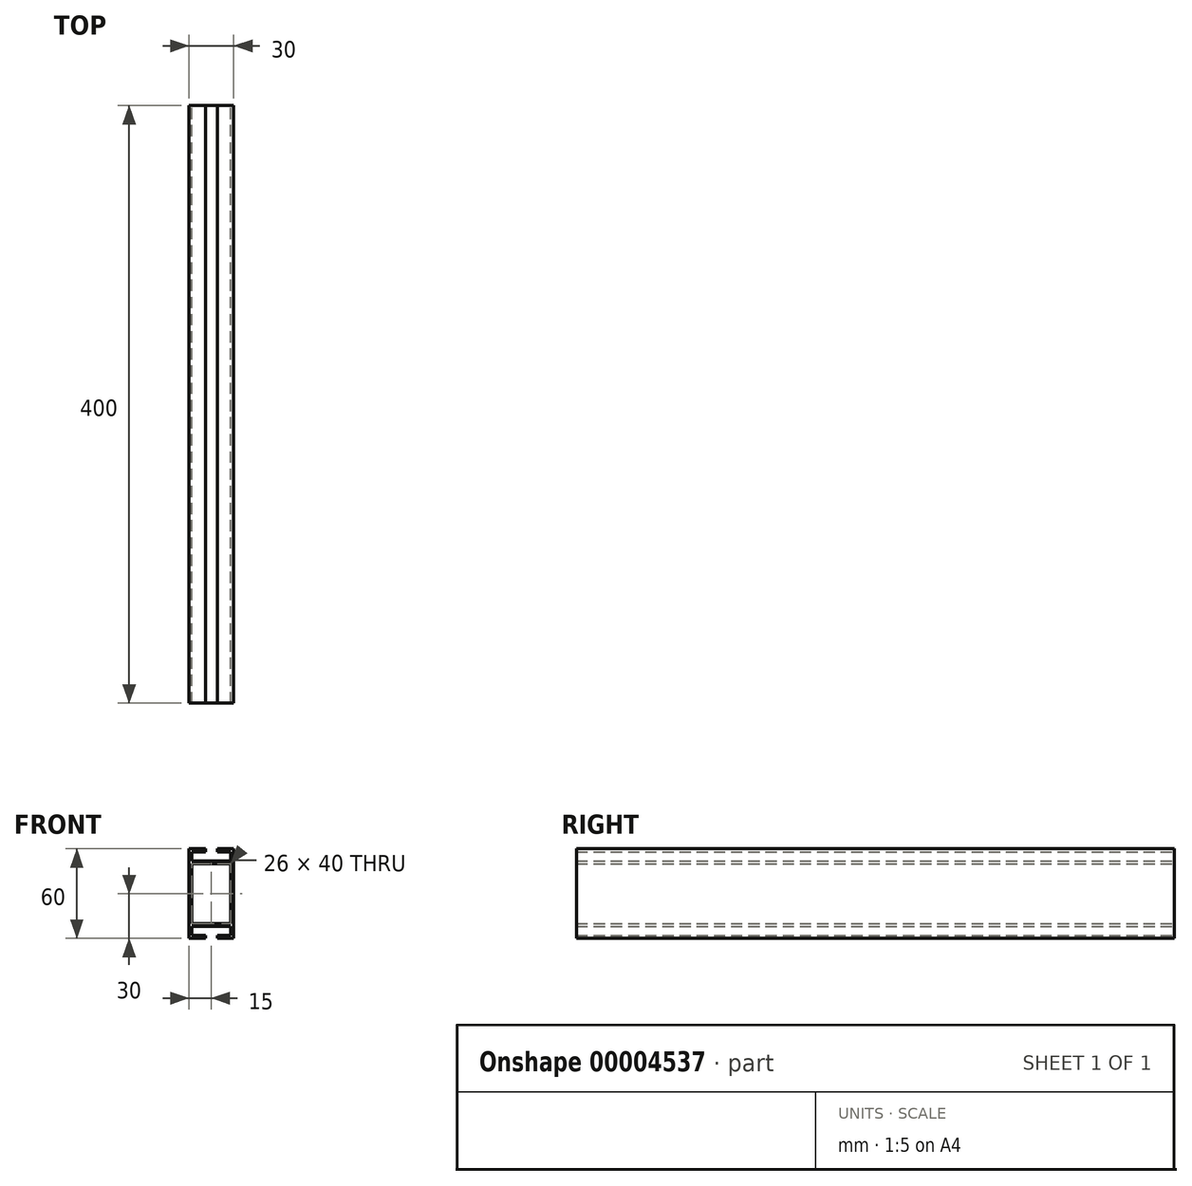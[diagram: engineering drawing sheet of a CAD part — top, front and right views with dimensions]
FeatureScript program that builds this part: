
annotation { "Feature Type Name" : "Feature", "Feature Type Description" : "" }
export const myFeature = defineFeature(function(context is Context, id is Id, definition is map)
    precondition{}
    {
        {
            var Q0;
            Q0=qCreatedBy(makeId("Front.planeOp"),FACE);
            var sketch = newSketch(context, id + "F0", { "sketchPlane" : qUnion([Q0])});
            skLineSegment(sketch, "E0.rect.bottom", {"start": v(15, 30) * mm, "end": v(4, 30) * mm});
            skLineSegment(sketch, "E0.rect.top", {"start": v(15, -30) * mm, "end": v(4, -30) * mm});
            skLineSegment(sketch, "E0.rect.left", {"start": v(15, 30) * mm, "end": v(15, -30) * mm});
            skLineSegment(sketch, "E0.rect.right", {"start": v(-15, 30) * mm, "end": v(-15, -30) * mm});
            skPoint(sketch, "E0.rect.middle", {"position": v(0, 0) * mm});
            skLineSegment(sketch, "E1.0", {"start": v(13, 28) * mm, "end": v(4, 28) * mm});
            skLineSegment(sketch, "E1.1", {"start": v(13, 28) * mm, "end": v(13, -22) * mm});
            skLineSegment(sketch, "E1.2", {"start": v(13, -28) * mm, "end": v(4, -28) * mm});
            skLineSegment(sketch, "E1.3", {"start": v(-13, 28) * mm, "end": v(-13, 22) * mm});
            skLineSegment(sketch, "E2.rect.bottom", {"start": v(13, 22) * mm, "end": v(-13, 22) * mm});
            skLineSegment(sketch, "E2.rect.top", {"start": v(13, -22) * mm, "end": v(-13, -22) * mm});
            skLineSegment(sketch, "E2.rect.left", {"start": v(13, 22) * mm, "end": v(13, -20) * mm});
            skLineSegment(sketch, "E2.rect.right", {"start": v(-13, 22) * mm, "end": v(-13, -22) * mm});
            skLineSegment(sketch, "E3.0", {"start": v(13, 20) * mm, "end": v(-13, 20) * mm});
            skLineSegment(sketch, "E4.0", {"start": v(13, -20) * mm, "end": v(4, -20) * mm});
            skLineSegment(sketch, "E5.rect.left", {"start": v(-4, 30) * mm, "end": v(-4, 28) * mm});
            skLineSegment(sketch, "E5.rect.right", {"start": v(4, 30) * mm, "end": v(4, 27.97) * mm});
            skLineSegment(sketch, "E6", {"start": v(-4, 30) * mm, "end": v(-15, 30) * mm});
            skLineSegment(sketch, "E7", {"start": v(-4, 28) * mm, "end": v(-13, 28) * mm});
            skLineSegment(sketch, "E8", {"start": v(-4, -20) * mm, "end": v(-13, -20) * mm});
            skLineSegment(sketch, "E9", {"start": v(-4, -28) * mm, "end": v(-4, -30) * mm});
            skLineSegment(sketch, "E10", {"start": v(4, -28) * mm, "end": v(4, -30) * mm});
            skLineSegment(sketch, "E11", {"start": v(4, -20) * mm, "end": v(-4, -20) * mm});
            skLineSegment(sketch, "E12", {"start": v(-4, -30) * mm, "end": v(-15, -30) * mm});
            skLineSegment(sketch, "E13", {"start": v(-4, -28) * mm, "end": v(-13, -28) * mm});
            skLineSegment(sketch, "E14", {"start": v(-13, 20) * mm, "end": v(-13, -20) * mm});
            skLineSegment(sketch, "E15", {"start": v(-13, -22) * mm, "end": v(-13, -22) * mm});
            skLineSegment(sketch, "E16", {"start": v(-13, -20) * mm, "end": v(-13, -28) * mm});
            skLineSegment(sketch, "E17", {"start": v(13, -22) * mm, "end": v(13, -28) * mm});
            skLineSegment(sketch, "E18", {"start": v(13, -20) * mm, "end": v(13, -22) * mm});
            skSolve(sketch);
        }
        {
            var Q0;
            Q0=makeQuery(id+"F0.imprint","IMPRINT",FACE,{"disambiguationData":[TD([[makeQuery(id+"F0.imprint","IMPRINT",EDGE,{"derivedFrom":sQuery(id+"F0.wireOp",EDGE,"E0.rect.right")}),1.0]])]});
            var Q1;
            {var subQ2=sQuery(id+"F0.wireOp",EDGE,"E2.rect.bottom");Q1=makeQuery(id+"F0.imprint","IMPRINT",FACE,{"disambiguationData":[TD([[makeQuery(id+"F0.imprint","IMPRINT",EDGE,{"derivedFrom":subQ2}),1.0]])]});}
            var Q2;
            {var subQ3=sQuery(id+"F0.wireOp",EDGE,"E0.rect.bottom");Q2=makeQuery(id+"F0.imprint","IMPRINT",FACE,{"disambiguationData":[TD([[makeQuery(id+"F0.imprint","IMPRINT",EDGE,{"derivedFrom":subQ3}),1.0]])]});}
            var Q3;
            {var subQ2=sQuery(id+"F0.wireOp",EDGE,"E2.rect.top");Q3=makeQuery(id+"F0.imprint","IMPRINT",FACE,{"disambiguationData":[TD([[makeQuery(id+"F0.imprint","IMPRINT",EDGE,{"derivedFrom":subQ2}),-1.0]])]});}
            extrude(context, id + "F1", {"entities" : qUnion([Q0, Q1, Q2, Q3]), "depth" : 400 * mm});
        }
    });
